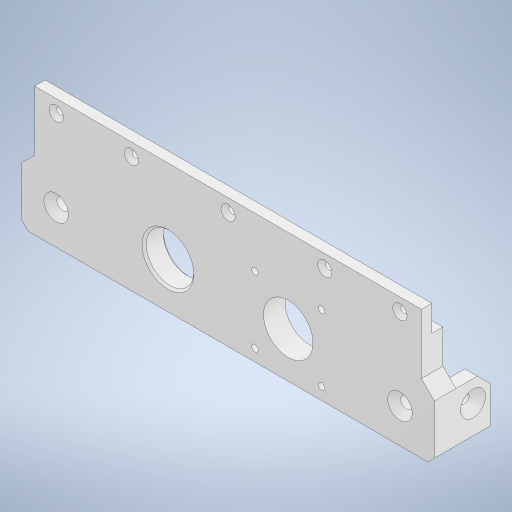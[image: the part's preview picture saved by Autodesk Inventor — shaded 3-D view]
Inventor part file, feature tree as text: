
AUTODESK INVENTOR PART (.ipt)
format: ipt  version: 2024.1 (Build 281209000, 209)  size: 489,472 bytes
history: native  units: in
note: dims shown in document units (in); Inventor stores cm internally (conversion verified against a paired STEP export)
features: extrude x18, sketch x18, chamfer x15
ambient origin geometry x8: Origin, YZ Plane, XZ Plane, XY Plane, X Axis, Y Axis, Z Axis, Center Point
bodies: Solid1 (feature_tree)
feature tree (51):
  extrude  "Extrusion1"  Depth=2.3622in
  extrude  "Extrusion4"  Depth=0.3937in
  extrude  "Extrusion5"  Depth=2.4409in
  extrude  "Extrusion6"  Depth=0.2362in
  extrude  "Extrusion7"  Depth=0.6299in
  chamfer  "Chamfer1"  Distance=0.7874in
  extrude  "Extrusion8"  Depth=0.0787in TaperAngle=45.0deg
  chamfer  "Chamfer2"  [1 undecoded]
  extrude  "Extrusion9"  Depth=0.0787in
  chamfer  "Chamfer3"  [1 undecoded]
  extrude  "Extrusion10"  Depth=0.0787in TaperAngle=45.0deg
  chamfer  "Chamfer4"  Distance=0.1181in
  extrude  "Extrusion11"  Depth=0.0787in
  chamfer  "Chamfer6"  Distance=0.1181in
  extrude  "Extrusion12"  Depth=0.0787in
  chamfer  "Chamfer7"  Distance=0.1181in
  extrude  "Extrusion13"  Depth=0.2362in
  extrude  "Extrusion14"  Depth=0.2362in
  extrude  "Extrusion15"  Depth=0.2362in
  chamfer  "Chamfer8"  Distance=0.2362in
  chamfer  "Chamfer9"  Distance=0.2362in
  extrude  "Extrusion16"  Depth=0.3937in
  chamfer  "Chamfer11"  Distance=0.3937in
  chamfer  "Chamfer12"  Distance=1.378in
  extrude  "Extrusion17"  Depth=0.0787in
  chamfer  "Chamfer13"  Distance=3.5433in
  chamfer  "Chamfer14"  [1 undecoded]
  chamfer  "Chamfer15"  Distance=0.0787in Angle=45.0deg
  extrude  "Extrusion18"  Depth=0.0787in
  chamfer  "Chamfer16"  Distance=0.3937in
  extrude  "Extrusion19"  Depth=0.0787in
  extrude  "Extrusion20"  TaperAngle=0.0deg  [1 undecoded]
  chamfer  "Chamfer18"  Distance=0.0787in Angle=45.0deg
  sketch  "Sketch1"  dims[d0=7.0866in d1=2.3622in]
  sketch  "Sketch4"  dims[d2=0.3937in d3=0.0in d16=0.9055in]
  sketch  "Sketch5"  dims[d17=0.8327in d18=2.4409in]
  sketch  "Sketch6"  dims[d19=0.0in d20=0.0in d21=0.2362in]
  sketch  "Sketch7"  dims[d22=0.6299in d23=0.0in d24=0.5551in]
  sketch  "Sketch8"  dims[d25=0.2362in]
  sketch  "Sketch9"  dims[d26=0.5551in]
  sketch  "Sketch10"  dims[d27=0.2362in d28=0.7874in d29=0.0in]
  sketch  "Sketch11"  dims[d30=0.0in d31=0.0in d32=0.1181in d33=0.0787in d34=45.0deg]
  sketch  "Sketch12"  dims[d35=0.8701in]
  sketch  "Sketch13"  dims[d36=0.8327in]
  sketch  "Sketch14"  dims[d37=2.4409in d38=0.0in d39=0.0in]
  sketch  "Sketch15"  dims[d40=0.0394in d41=0.0787in d42=45.0deg d43=0.1575in]
  sketch  "Sketch16"  dims[d44=0.3937in]
  sketch  "Sketch17"  dims[d45=0.1575in]
  sketch  "Sketch18"  dims[d46=0.3937in]
  sketch  "Sketch19"  dims[d47=0.315in]
  sketch  "Sketch20"  dims[d48=0.315in d49=0.0in d50=0.0in d51=0.1378in d52=0.0787in d53=45.0deg d54=0.1181in d55=0.1181in d56=0.1181in d57=0.1181in d58=0.1181in d59=0.2362in d60=0.2362in d61=0.2362in d62=0.2362in d63=0.2362in d64=0.3937in d65=0.3937in d66=1.378in d67=1.378in d68=3.5433in d69=0.0in d70=0.0in d71=0.0709in d72=0.0787in d73=45.0deg d77=0.1575in d78=0.3937in d79=0.315in d80=0.0in d81=0.0in d82=0.1181in d83=0.0787in d84=45.0deg d85=0.1181in d86=0.1181in d87=0.1181in d88=0.1181in d89=0.6102in d90=0.6102in d91=0.6102in d93=0.6102in d94=0.6102in d95=0.6102in d96=1.2205in d97=0.6102in d98=0.0in d99=0.0in d100=0.0709in d101=0.0787in d102=45.0deg d103=0.4764in d104=0.4764in d105=0.2008in d106=0.0in d107=0.0in d108=0.0in d109=0.0in d110=0.7913in d111=1.0236in d112=0.2362in d113=0.0in d114=0.2362in d115=0.0787in d116=45.0deg d117=0.1181in d118=0.0787in d119=45.0deg d123=0.1575in d124=0.3937in d125=0.315in d126=0.0in d127=0.0in d128=0.1496in d129=0.0787in d130=45.0deg d131=0.2362in d132=0.0787in d133=45.0deg d134=1.0236in d135=1.0276in d136=0.2362in d137=0.0in d138=0.2362in d139=0.0787in d140=45.0deg d141=0.1181in d142=0.0787in d143=45.0deg d144=0.2362in d145=0.0787in d146=45.0deg d147=0.0in d148=0.0in d149=0.1378in d150=0.0787in d151=45.0deg d152=0.2126in d153=0.2126in d154=0.3937in d155=0.6299in d156=0.3937in d157=0.6299in d158=0.0in d159=0.0in d164=0.0079in d165=0.0079in d166=0.0079in d167=0.3937in d168=0.0in d169=0.1181in d170=0.0787in d171=45.0deg]
note: 4 required parameter values undecoded (feature->parameter linkage not recoverable at this tier; creation-order binding heuristic only, values carry confidence <= 0.55)
